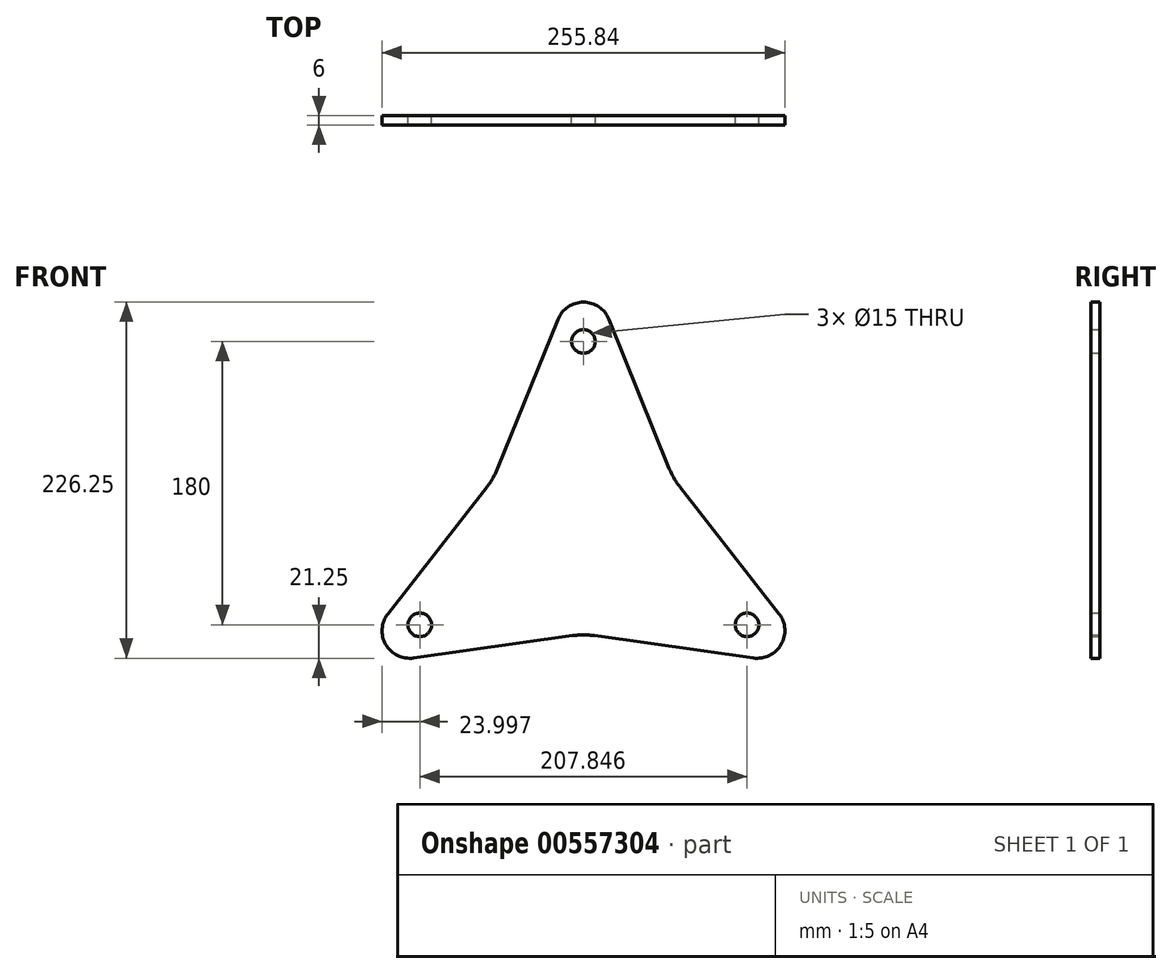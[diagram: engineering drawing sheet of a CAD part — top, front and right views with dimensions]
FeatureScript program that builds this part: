
annotation { "Feature Type Name" : "Feature", "Feature Type Description" : "" }
export const myFeature = defineFeature(function(context is Context, id is Id, definition is map)
    precondition{}
    {
        {
            var Q0;
            Q0=qCreatedBy(makeId("Front.planeOp"),FACE);
            var sketch = newSketch(context, id + "F0", { "sketchPlane" : qUnion([Q0])});
            skCircle(sketch, "E0", {"center": v(0, 0) * mm, "radius": 145 * mm});
            skLineSegment(sketch, "E1", {"start": v(0, 0) * mm, "end": v(0, 145) * mm});
            skLineSegment(sketch, "E2", {"start": v(0, 0) * mm, "end": v(0, -145) * mm});
            skLineSegment(sketch, "E3", {"start": v(0, -145) * mm, "end": v(0, 0) * mm});
            skLineSegment(sketch, "E4", {"start": v(0, 0) * mm, "end": v(125.57, -72.5) * mm});
            skLineSegment(sketch, "E5", {"start": v(0, 0) * mm, "end": v(-125.57, -72.5) * mm});
            skLineSegment(sketch, "E6", {"start": v(0, 0) * mm, "end": v(-125.57, 72.5) * mm});
            skCircle(sketch, "E7", {"center": v(0, 0) * mm, "radius": 120 * mm});
            skCircle(sketch, "E8", {"center": v(0, 120) * mm, "radius": 7.5 * mm});
            skPoint(sketch, "E9.visualSharp", {"position": v(0, 145) * mm});
            skCircle(sketch, "E10", {"center": v(-103.92, -60) * mm, "radius": 7.5 * mm});
            skCircle(sketch, "E11", {"center": v(103.92, -60) * mm, "radius": 7.5 * mm});
            skLineSegment(sketch, "E12", {"start": v(0, -65.9) * mm, "end": v(-107.98, -81.08) * mm});
            skLineSegment(sketch, "E13", {"start": v(0, -65.9) * mm, "end": v(107.98, -81.08) * mm});
            skLineSegment(sketch, "E14", {"start": v(0, 0) * mm, "end": v(103.92, 60) * mm});
            skLineSegment(sketch, "E15", {"start": v(57.07, 32.95) * mm, "end": v(16.23, 134.06) * mm});
            skLineSegment(sketch, "E16", {"start": v(-16.23, 134.06) * mm, "end": v(-57.07, 32.95) * mm});
            skLineSegment(sketch, "E17", {"start": v(124.2, -52.98) * mm, "end": v(57.07, 32.95) * mm});
            skLineSegment(sketch, "E18", {"start": v(-57.07, 32.95) * mm, "end": v(-124.2, -52.98) * mm});
            skArc(sketch, "E19", {"start": v(16.23, 134.06) * mm, "mid": v(0, 145) * mm, "end": v(-16.23, 134.06) * mm});
            skArc(sketch, "E20", {"start": v(107.98, -81.08) * mm, "mid": v(125.57, -72.5) * mm, "end": v(124.2, -52.98) * mm});
            skArc(sketch, "E21", {"start": v(-124.2, -52.98) * mm, "mid": v(-125.57, -72.5) * mm, "end": v(-107.98, -81.08) * mm});
            skSolve(sketch);
        }
        {
            var Q0;
            {var subQ0=sQuery(id+"F0.wireOp",EDGE,"E11");var subQ3=sQuery(id+"F0.wireOp",EDGE,"E7");var subQ4=makeQuery(id+"F0.imprint","INTERSECT",VERTEX,{"disambiguationData":[OD(1.0)],"derivedFrom":[subQ3,subQ0]});Q0=makeQuery(id+"F0.imprint","IMPRINT",FACE,{"disambiguationData":[TD([[makeQuery(id+"F0.imprint","IMPRINT",EDGE,{"disambiguationData":[TD([[subQ4,-1.0]])],"derivedFrom":subQ3}),1.0]])]});}
            var Q1;
            {var subQ3=sQuery(id+"F0.wireOp",EDGE,"E7");var subQ5=sQuery(id+"F0.wireOp",EDGE,"E11");var subQ8=makeQuery(id+"F0.imprint","INTERSECT",VERTEX,{"disambiguationData":[OD(1.0)],"derivedFrom":[subQ3,subQ5]});Q1=makeQuery(id+"F0.imprint","IMPRINT",FACE,{"disambiguationData":[TD([[makeQuery(id+"F0.imprint","IMPRINT",EDGE,{"disambiguationData":[TD([[subQ8,-1.0]])],"derivedFrom":subQ3}),-1.0]])]});}
            var Q2;
            {var subQ3=sQuery(id+"F0.wireOp",EDGE,"E7");var subQ7=sQuery(id+"F0.wireOp",EDGE,"E13");var subQ8=makeQuery(id+"F0.imprint","INTERSECT",VERTEX,{"derivedFrom":[subQ3,subQ7]});Q2=makeQuery(id+"F0.imprint","IMPRINT",FACE,{"disambiguationData":[TD([[makeQuery(id+"F0.imprint","IMPRINT",EDGE,{"disambiguationData":[TD([[subQ8,-1.0]])],"derivedFrom":subQ3}),1.0]])]});}
            var Q3;
            {var subQ0=sQuery(id+"F0.wireOp",EDGE,"E10");var subQ3=sQuery(id+"F0.wireOp",EDGE,"E7");var subQ4=makeQuery(id+"F0.imprint","INTERSECT",VERTEX,{"disambiguationData":[OD(1.0)],"derivedFrom":[subQ3,subQ0]});Q3=makeQuery(id+"F0.imprint","IMPRINT",FACE,{"disambiguationData":[TD([[makeQuery(id+"F0.imprint","IMPRINT",EDGE,{"disambiguationData":[TD([[subQ4,-1.0]])],"derivedFrom":subQ3}),1.0]])]});}
            var Q4;
            {var subQ3=sQuery(id+"F0.wireOp",EDGE,"E7");var subQ5=sQuery(id+"F0.wireOp",EDGE,"E18");var subQ6=makeQuery(id+"F0.imprint","INTERSECT",VERTEX,{"derivedFrom":[subQ3,subQ5]});Q4=makeQuery(id+"F0.imprint","IMPRINT",FACE,{"disambiguationData":[TD([[makeQuery(id+"F0.imprint","IMPRINT",EDGE,{"disambiguationData":[TD([[subQ6,-1.0]])],"derivedFrom":subQ3}),1.0]])]});}
            var Q5;
            {var subQ1=sQuery(id+"F0.wireOp",EDGE,"E18");var subQ3=sQuery(id+"F0.wireOp",EDGE,"E7");var subQ4=makeQuery(id+"F0.imprint","INTERSECT",VERTEX,{"derivedFrom":[subQ3,subQ1]});Q5=makeQuery(id+"F0.imprint","IMPRINT",FACE,{"disambiguationData":[TD([[makeQuery(id+"F0.imprint","IMPRINT",EDGE,{"disambiguationData":[TD([[subQ4,-1.0]])],"derivedFrom":subQ3}),-1.0]])]});}
            var Q6;
            {var subQ0=sQuery(id+"F0.wireOp",EDGE,"E10");var subQ3=sQuery(id+"F0.wireOp",EDGE,"E7");var subQ4=makeQuery(id+"F0.imprint","INTERSECT",VERTEX,{"disambiguationData":[OD(1.0)],"derivedFrom":[subQ3,subQ0]});Q6=makeQuery(id+"F0.imprint","IMPRINT",FACE,{"disambiguationData":[TD([[makeQuery(id+"F0.imprint","IMPRINT",EDGE,{"disambiguationData":[TD([[subQ4,-1.0]])],"derivedFrom":subQ3}),-1.0]])]});}
            var Q7;
            {var subQ0=sQuery(id+"F0.wireOp",EDGE,"E8");var subQ3=sQuery(id+"F0.wireOp",EDGE,"E7");var subQ4=makeQuery(id+"F0.imprint","INTERSECT",VERTEX,{"disambiguationData":[OD(1.0)],"derivedFrom":[subQ3,subQ0]});Q7=makeQuery(id+"F0.imprint","IMPRINT",FACE,{"disambiguationData":[TD([[makeQuery(id+"F0.imprint","IMPRINT",EDGE,{"disambiguationData":[TD([[subQ4,-1.0]])],"derivedFrom":subQ3}),1.0]])]});}
            var Q8;
            {var subQ3=sQuery(id+"F0.wireOp",EDGE,"E7");var subQ5=sQuery(id+"F0.wireOp",EDGE,"E8");var subQ8=makeQuery(id+"F0.imprint","INTERSECT",VERTEX,{"disambiguationData":[OD(1.0)],"derivedFrom":[subQ3,subQ5]});Q8=makeQuery(id+"F0.imprint","IMPRINT",FACE,{"disambiguationData":[TD([[makeQuery(id+"F0.imprint","IMPRINT",EDGE,{"disambiguationData":[TD([[subQ8,-1.0]])],"derivedFrom":subQ3}),-1.0]])]});}
            var Q9;
            {var subQ1=sQuery(id+"F0.wireOp",EDGE,"E15");var subQ3=sQuery(id+"F0.wireOp",EDGE,"E7");var subQ4=makeQuery(id+"F0.imprint","INTERSECT",VERTEX,{"derivedFrom":[subQ3,subQ1]});Q9=makeQuery(id+"F0.imprint","IMPRINT",FACE,{"disambiguationData":[TD([[makeQuery(id+"F0.imprint","IMPRINT",EDGE,{"disambiguationData":[TD([[subQ4,-1.0]])],"derivedFrom":subQ3}),-1.0]])]});}
            var Q10;
            {var subQ1=sQuery(id+"F0.wireOp",EDGE,"E13");var subQ3=sQuery(id+"F0.wireOp",EDGE,"E7");var subQ4=makeQuery(id+"F0.imprint","INTERSECT",VERTEX,{"derivedFrom":[subQ3,subQ1]});Q10=makeQuery(id+"F0.imprint","IMPRINT",FACE,{"disambiguationData":[TD([[makeQuery(id+"F0.imprint","IMPRINT",EDGE,{"disambiguationData":[TD([[subQ4,-1.0]])],"derivedFrom":subQ3}),-1.0]])]});}
            var Q11;
            {var subQ3=sQuery(id+"F0.wireOp",EDGE,"E15");var subQ5=sQuery(id+"F0.wireOp",EDGE,"E7");var subQ6=makeQuery(id+"F0.imprint","INTERSECT",VERTEX,{"derivedFrom":[subQ5,subQ3]});Q11=makeQuery(id+"F0.imprint","IMPRINT",FACE,{"disambiguationData":[TD([[makeQuery(id+"F0.imprint","IMPRINT",EDGE,{"disambiguationData":[TD([[subQ6,-1.0]])],"derivedFrom":subQ5}),1.0]])]});}
            extrude(context, id + "F1", {"entities" : qUnion([Q0, Q1, Q2, Q3, Q4, Q5, Q6, Q7, Q8, Q9, Q10, Q11]), "depth" : 6 * mm, "offsetDistance" : 25 * mm});
        }
        {
            var Q0;
            Q0=makeQuery(id+"F1.opExtrude","SWEPT_EDGE",EDGE,{"disambiguationData":[OSD([sQuery(id+"F0.wireOp",EDGE,"E6"),sQuery(id+"F0.wireOp",EDGE,"E16"),sQuery(id+"F0.wireOp",EDGE,"E18")])]});
            fillet(context, id + "F2", {"entities" : qUnion([Q0]), "radius" : 50 * mm, "tangentPropagation" : true, "allowEdgeOverflow" : false});
        }
        {
            var Q0;
            Q0=makeQuery(id+"F1.opExtrude","SWEPT_EDGE",EDGE,{"disambiguationData":[OSD([sQuery(id+"F0.wireOp",EDGE,"E3"),sQuery(id+"F0.wireOp",EDGE,"E12"),sQuery(id+"F0.wireOp",EDGE,"E13")])]});
            fillet(context, id + "F3", {"entities" : qUnion([Q0]), "radius" : 50 * mm, "tangentPropagation" : true, "allowEdgeOverflow" : false});
        }
        {
            var Q0;
            Q0=makeQuery(id+"F1.opExtrude","SWEPT_EDGE",EDGE,{"disambiguationData":[OSD([sQuery(id+"F0.wireOp",EDGE,"E14"),sQuery(id+"F0.wireOp",EDGE,"E15"),sQuery(id+"F0.wireOp",EDGE,"E17")])]});
            fillet(context, id + "F4", {"entities" : qUnion([Q0]), "radius" : 50 * mm, "tangentPropagation" : true, "allowEdgeOverflow" : false});
        }
    });
